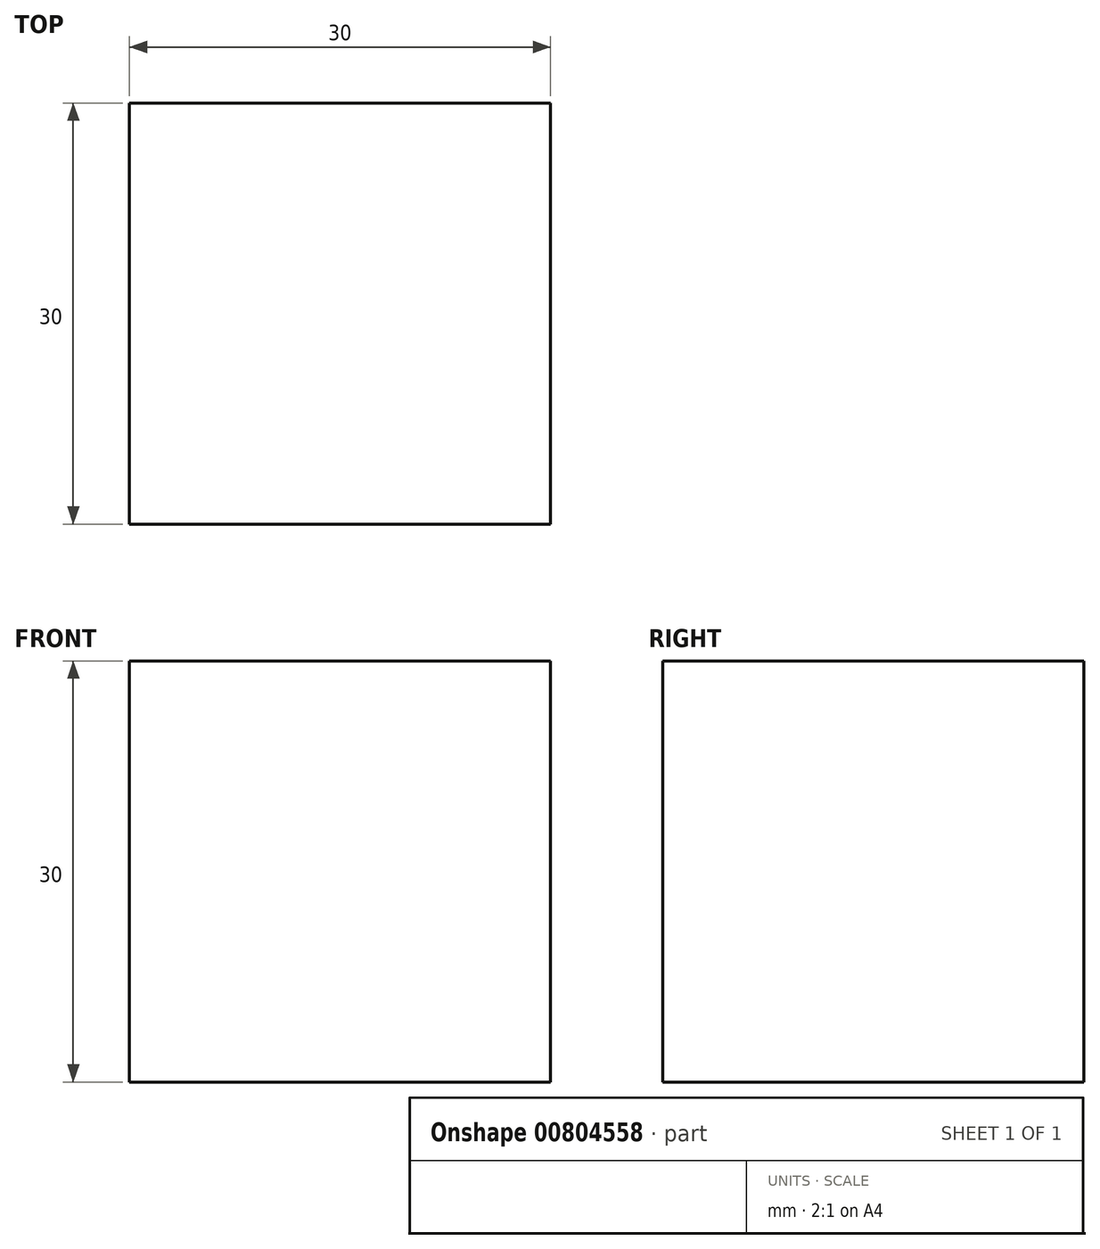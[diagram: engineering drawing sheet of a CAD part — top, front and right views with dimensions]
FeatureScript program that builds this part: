
annotation { "Feature Type Name" : "Feature", "Feature Type Description" : "" }
export const myFeature = defineFeature(function(context is Context, id is Id, definition is map)
    precondition{}
    {
        {
            var Q0;
            Q0=qCreatedBy(makeId("Top.planeOp"),FACE);
            var sketch = newSketch(context, id + "F0", { "sketchPlane" : qUnion([Q0])});
            skLineSegment(sketch, "E0.bottom", {"start": v(15, -15) * mm, "end": v(-15, -15) * mm});
            skLineSegment(sketch, "E0.top", {"start": v(15, 15) * mm, "end": v(-15, 15) * mm});
            skLineSegment(sketch, "E0.left", {"start": v(15, -15) * mm, "end": v(15, 15) * mm});
            skLineSegment(sketch, "E0.right", {"start": v(-15, -15) * mm, "end": v(-15, 15) * mm});
            skPoint(sketch, "E0.middle", {"position": v(0, 0) * mm});
            skSolve(sketch);
        }
        {
            var Q0;
            Q0 = qSketchRegion(id + "F0", true);
            extrude(context, id + "F1", {"entities" : qUnion([Q0]), "depth" : 30 * mm, "offsetDistance" : 25 * mm});
        }
    });
